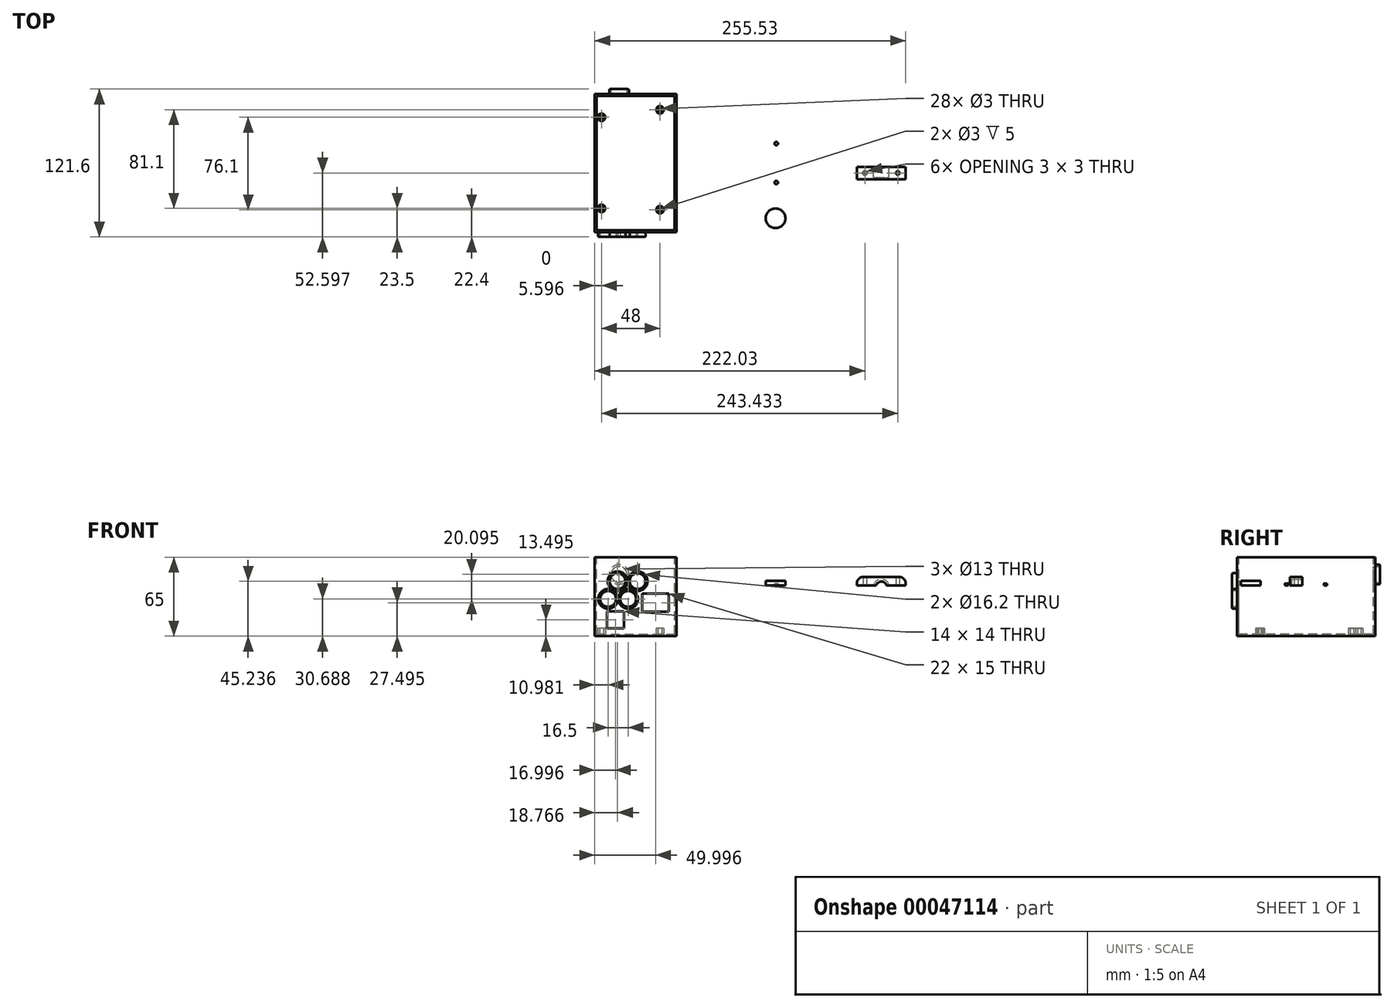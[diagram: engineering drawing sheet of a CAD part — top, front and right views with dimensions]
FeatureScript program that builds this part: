
annotation { "Feature Type Name" : "Feature", "Feature Type Description" : "" }
export const myFeature = defineFeature(function(context is Context, id is Id, definition is map)
    precondition{}
    {
        {
            assignVariable(context, id + "F0", {"name" : "width", "anyValue" : 1.6});
        }
        {
            var Q0;
            Q0=qCreatedBy(makeId("Front.planeOp"),FACE);
            var sketch = newSketch(context, id + "F1", { "sketchPlane" : qUnion([Q0])});
            skLineSegment(sketch, "E0.bottom", {"start": v(-41.87, 23.3) * mm, "end": v(25.33, 23.3) * mm});
            skLineSegment(sketch, "E0.top", {"start": v(-41.87, -41.7) * mm, "end": v(25.33, -41.7) * mm});
            skLineSegment(sketch, "E0.left", {"start": v(-41.87, 23.3) * mm, "end": v(-41.87, -41.7) * mm});
            skLineSegment(sketch, "E0.right", {"start": v(25.33, 23.3) * mm, "end": v(25.33, -41.7) * mm});
            skSolve(sketch);
        }
        {
            var Q0;
            Q0 = qSketchRegion(id + "F1", true);
            extrude(context, id + "F2", {"entities" : qUnion([Q0]), "depth" : 113.6 * mm});
        }
        {
            var Q0;
            Q0=makeQuery(id+"F2.opExtrude","SWEPT_FACE",FACE,{"disambiguationData":[OSD([sQuery(id+"F1.wireOp",EDGE,"E0.bottom")])]});
            var sketch = newSketch(context, id + "F3", { "sketchPlane" : qUnion([Q0])});
            skLineSegment(sketch, "E1.bottom", {"start": v(-40.27, -1.6) * mm, "end": v(23.73, -1.6) * mm});
            skLineSegment(sketch, "E1.top", {"start": v(-40.27, -112) * mm, "end": v(23.73, -112) * mm});
            skLineSegment(sketch, "E1.left", {"start": v(-40.27, -1.6) * mm, "end": v(-40.27, -112) * mm});
            skLineSegment(sketch, "E1.right", {"start": v(23.73, -1.6) * mm, "end": v(23.73, -112) * mm});
            skSolve(sketch);
        }
        {
            var Q0;
            Q0 = qSketchRegion(id + "F3", true);
            extrude(context, id + "F4", {"entities" : qUnion([Q0]), "operationType" : NewBodyOperationType.REMOVE, "oppositeDirection" : true, "depth" : (65 - getVariable(context, 'width')) * mm});
        }
        {
            var Q0;
            Q0=makeQuery(id+"F2.opExtrude","CAP_FACE",FACE,{"disambiguationData":[OSD([sQuery(id+"F1.wireOp",EDGE,"E0.bottom"),sQuery(id+"F1.wireOp",EDGE,"E0.top"),sQuery(id+"F1.wireOp",EDGE,"E0.left"),sQuery(id+"F1.wireOp",EDGE,"E0.right")])],"isStart":false});
            var sketch = newSketch(context, id + "F5", { "sketchPlane" : qUnion([Q0])});
            skLineSegment(sketch, "E2.bottom", {"start": v(-31.87, -21.2) * mm, "end": v(-17.87, -21.2) * mm});
            skLineSegment(sketch, "E2.top", {"start": v(-31.87, -35.2) * mm, "end": v(-17.87, -35.2) * mm});
            skLineSegment(sketch, "E2.left", {"start": v(-31.87, -21.2) * mm, "end": v(-31.87, -35.2) * mm});
            skLineSegment(sketch, "E2.right", {"start": v(-17.87, -21.2) * mm, "end": v(-17.87, -35.2) * mm});
            skLineSegment(sketch, "E3.bottom", {"start": v(-2.87, -6.7) * mm, "end": v(19.13, -6.7) * mm});
            skLineSegment(sketch, "E3.top", {"start": v(-2.87, -21.7) * mm, "end": v(19.13, -21.7) * mm});
            skLineSegment(sketch, "E3.left", {"start": v(-2.87, -6.7) * mm, "end": v(-2.87, -21.7) * mm});
            skLineSegment(sketch, "E3.right", {"start": v(19.13, -6.7) * mm, "end": v(19.13, -21.7) * mm});
            skCircle(sketch, "E4", {"center": v(-30.89, -11) * mm, "radius": 6.5 * mm});
            skCircle(sketch, "E5", {"center": v(-14.39, -11) * mm, "radius": 6.5 * mm});
            skCircle(sketch, "E6.MirrorC", {"center": v(-6.6, 3.55) * mm, "radius": 6.5 * mm});
            skCircle(sketch, "E7.MirrorC", {"center": v(-23.1, 3.55) * mm, "radius": 6.5 * mm});
            skCircle(sketch, "E8.0", {"center": v(-30.89, -11) * mm, "radius": 8.1 * mm});
            skCircle(sketch, "E9.0", {"center": v(-14.39, -11) * mm, "radius": 8.1 * mm});
            skCircle(sketch, "E10.0", {"center": v(-23.1, 3.55) * mm, "radius": 8.1 * mm});
            skCircle(sketch, "E11.0", {"center": v(-6.6, 3.55) * mm, "radius": 8.1 * mm});
            skSolve(sketch);
        }
        {
            var Q0;
            Q0=makeQuery(id+"F5.imprint","IMPRINT",FACE,{"disambiguationData":[TD([[makeQuery(id+"F5.imprint","IMPRINT",EDGE,{"derivedFrom":sQuery(id+"F5.wireOp",EDGE,"E3.bottom")}),-1.0]])]});
            var Q1;
            Q1=makeQuery(id+"F5.imprint","IMPRINT",FACE,{"disambiguationData":[TD([[makeQuery(id+"F5.imprint","IMPRINT",EDGE,{"derivedFrom":sQuery(id+"F5.wireOp",EDGE,"E2.bottom")}),-1.0]])]});
            var Q2;
            Q2=makeQuery(id+"F5.imprint","IMPRINT",FACE,{"disambiguationData":[TD([[makeQuery(id+"F5.imprint","IMPRINT",EDGE,{"derivedFrom":sQuery(id+"F5.wireOp",EDGE,"E5")}),1.0]])]});
            var Q3;
            Q3=makeQuery(id+"F5.imprint","IMPRINT",FACE,{"disambiguationData":[TD([[makeQuery(id+"F5.imprint","IMPRINT",EDGE,{"derivedFrom":sQuery(id+"F5.wireOp",EDGE,"E6.MirrorC")}),-1.0]])]});
            var Q4;
            Q4=makeQuery(id+"F5.imprint","IMPRINT",FACE,{"disambiguationData":[TD([[makeQuery(id+"F5.imprint","IMPRINT",EDGE,{"derivedFrom":sQuery(id+"F5.wireOp",EDGE,"E7.MirrorC")}),-1.0]])]});
            var Q5;
            Q5=makeQuery(id+"F5.imprint","IMPRINT",FACE,{"disambiguationData":[TD([[makeQuery(id+"F5.imprint","IMPRINT",EDGE,{"derivedFrom":sQuery(id+"F5.wireOp",EDGE,"E4")}),1.0]])]});
            extrude(context, id + "F6", {"entities" : qUnion([Q0, Q1, Q2, Q3, Q4, Q5]), "operationType" : NewBodyOperationType.REMOVE, "endBound" : BoundingType.UP_TO_NEXT, "oppositeDirection" : true, "depth" : 25 * mm});
        }
        {
            var Q0;
            Q0=makeQuery(id+"F5.imprint","IMPRINT",FACE,{"disambiguationData":[TD([[makeQuery(id+"F5.imprint","IMPRINT",EDGE,{"derivedFrom":sQuery(id+"F5.wireOp",EDGE,"E7.MirrorC")}),1.0]])]});
            var Q1;
            Q1=makeQuery(id+"F5.imprint","IMPRINT",FACE,{"disambiguationData":[TD([[makeQuery(id+"F5.imprint","IMPRINT",EDGE,{"derivedFrom":sQuery(id+"F5.wireOp",EDGE,"E6.MirrorC")}),1.0]])]});
            var Q2;
            Q2=makeQuery(id+"F5.imprint","IMPRINT",FACE,{"disambiguationData":[TD([[makeQuery(id+"F5.imprint","IMPRINT",EDGE,{"derivedFrom":sQuery(id+"F5.wireOp",EDGE,"E5")}),-1.0]])]});
            var Q3;
            Q3=makeQuery(id+"F5.imprint","IMPRINT",FACE,{"disambiguationData":[TD([[makeQuery(id+"F5.imprint","IMPRINT",EDGE,{"derivedFrom":sQuery(id+"F5.wireOp",EDGE,"E4")}),-1.0]])]});
            extrude(context, id + "F7", {"entities" : qUnion([Q0, Q1, Q2, Q3]), "operationType" : NewBodyOperationType.ADD, "depth" : 4 * mm});
        }
        {
            var Q0;
            Q0=makeQuery(id+"F7.opExtrude","CAP_FACE",FACE,{"disambiguationData":[OSD([sQuery(id+"F5.wireOp",EDGE,"E4"),sQuery(id+"F5.wireOp",EDGE,"E8.0")])],"isStart":false});
            var Q1;
            Q1=makeQuery(id+"F7.opExtrude","CAP_FACE",FACE,{"disambiguationData":[OSD([sQuery(id+"F5.wireOp",EDGE,"E7.MirrorC"),sQuery(id+"F5.wireOp",EDGE,"E10.0")])],"isStart":false});
            var Q2;
            Q2=makeQuery(id+"F7.opExtrude","CAP_FACE",FACE,{"disambiguationData":[OSD([sQuery(id+"F5.wireOp",EDGE,"E6.MirrorC"),sQuery(id+"F5.wireOp",EDGE,"E11.0")])],"isStart":false});
            var Q3;
            Q3=makeQuery(id+"F7.opExtrude","CAP_FACE",FACE,{"disambiguationData":[OSD([sQuery(id+"F5.wireOp",EDGE,"E5"),sQuery(id+"F5.wireOp",EDGE,"E9.0")])],"isStart":false});
            fillet(context, id + "F8", {"entities" : qUnion([Q0, Q1, Q2, Q3]), "radius" : 0.8 * mm, "tangentPropagation" : true, "allowEdgeOverflow" : false});
        }
        {
            var Q0;
            Q0=makeQuery(id+"F2.opExtrude","CAP_FACE",FACE,{"disambiguationData":[OSD([sQuery(id+"F1.wireOp",EDGE,"E0.bottom"),sQuery(id+"F1.wireOp",EDGE,"E0.top"),sQuery(id+"F1.wireOp",EDGE,"E0.left"),sQuery(id+"F1.wireOp",EDGE,"E0.right")])],"isStart":true});
            var sketch = newSketch(context, id + "F9", { "sketchPlane" : qUnion([Q0])});
            skCircle(sketch, "E12", {"center": v(21.87, 9.1) * mm, "radius": 6.5 * mm});
            skCircle(sketch, "E13.0", {"center": v(21.87, 9.1) * mm, "radius": 8.1 * mm});
            skSolve(sketch);
        }
        {
            var Q0;
            Q0=makeQuery(id+"F9.imprint","IMPRINT",FACE,{"disambiguationData":[TD([[makeQuery(id+"F9.imprint","IMPRINT",EDGE,{"derivedFrom":sQuery(id+"F9.wireOp",EDGE,"E12")}),1.0]])]});
            extrude(context, id + "F10", {"entities" : qUnion([Q0]), "operationType" : NewBodyOperationType.REMOVE, "endBound" : BoundingType.UP_TO_NEXT, "oppositeDirection" : true, "depth" : 25 * mm});
        }
        {
            var Q0;
            Q0=makeQuery(id+"F4.boolean.opBoolean","COPY",FACE,{"derivedFrom":makeQuery(id+"F4.opExtrude","CAP_FACE",FACE,{"disambiguationData":[OSD([sQuery(id+"F3.wireOp",EDGE,"E1.bottom"),sQuery(id+"F3.wireOp",EDGE,"E1.top"),sQuery(id+"F3.wireOp",EDGE,"E1.left"),sQuery(id+"F3.wireOp",EDGE,"E1.right")])],"isStart":false})});
            var sketch = newSketch(context, id + "F11", { "sketchPlane" : qUnion([Q0])});
            skCircle(sketch, "E14", {"center": v(-36.27, -94.1) * mm, "radius": 1.5 * mm});
            skCircle(sketch, "E15.0", {"center": v(-36.27, -94.1) * mm, "radius": 3.1 * mm});
            skCircle(sketch, "E16", {"center": v(11.73, -95.2) * mm, "radius": 1.5 * mm});
            skCircle(sketch, "E17.0", {"center": v(11.73, -95.2) * mm, "radius": 3.1 * mm});
            skCircle(sketch, "E18.0", {"center": v(-36.27, -19.1) * mm, "radius": 3.1 * mm});
            skCircle(sketch, "E19", {"center": v(-36.27, -19.1) * mm, "radius": 1.5 * mm});
            skCircle(sketch, "E20.0", {"center": v(11.73, -13) * mm, "radius": 3.1 * mm});
            skCircle(sketch, "E21", {"center": v(11.73, -13) * mm, "radius": 1.5 * mm});
            skSolve(sketch);
        }
        {
            var Q0;
            Q0 = qSketchRegion(id + "F11", true);
            extrude(context, id + "F12", {"entities" : qUnion([Q0]), "operationType" : NewBodyOperationType.ADD, "depth" : 5 * mm});
        }
        {
            var Q0;
            Q0=makeQuery(id+"F12.boolean.opBoolean","SPLIT",FACE,{"disambiguationData":[TD([makeQuery(id+"F12.opExtrude","SWEPT_FACE",FACE,{"disambiguationData":[OSD([sQuery(id+"F11.wireOp",EDGE,"E14")])]})])],"derivedFrom":makeQuery(id+"F4.boolean.opBoolean","COPY",FACE,{"derivedFrom":makeQuery(id+"F4.opExtrude","CAP_FACE",FACE,{"disambiguationData":[OSD([sQuery(id+"F3.wireOp",EDGE,"E1.bottom"),sQuery(id+"F3.wireOp",EDGE,"E1.top"),sQuery(id+"F3.wireOp",EDGE,"E1.left"),sQuery(id+"F3.wireOp",EDGE,"E1.right")])],"isStart":false})})});
            var Q1;
            Q1=makeQuery(id+"F12.boolean.opBoolean","SPLIT",FACE,{"disambiguationData":[TD([makeQuery(id+"F12.opExtrude","SWEPT_FACE",FACE,{"disambiguationData":[OSD([sQuery(id+"F11.wireOp",EDGE,"E21")])]})])],"derivedFrom":makeQuery(id+"F4.boolean.opBoolean","COPY",FACE,{"derivedFrom":makeQuery(id+"F4.opExtrude","CAP_FACE",FACE,{"disambiguationData":[OSD([sQuery(id+"F3.wireOp",EDGE,"E1.bottom"),sQuery(id+"F3.wireOp",EDGE,"E1.top"),sQuery(id+"F3.wireOp",EDGE,"E1.left"),sQuery(id+"F3.wireOp",EDGE,"E1.right")])],"isStart":false})})});
            extrude(context, id + "F13", {"entities" : qUnion([Q0, Q1]), "operationType" : NewBodyOperationType.REMOVE, "endBound" : BoundingType.UP_TO_NEXT, "oppositeDirection" : true, "depth" : 25 * mm});
        }
        {
            var Q0;
            Q0=makeQuery(id+"F9.imprint","IMPRINT",FACE,{"disambiguationData":[TD([[makeQuery(id+"F9.imprint","IMPRINT",EDGE,{"derivedFrom":sQuery(id+"F9.wireOp",EDGE,"E12")}),-1.0]])]});
            extrude(context, id + "F14", {"entities" : qUnion([Q0]), "operationType" : NewBodyOperationType.ADD, "depth" : 4 * mm});
        }
        {
            var Q0;
            Q0=makeQuery(id+"F14.opExtrude","CAP_FACE",FACE,{"disambiguationData":[OSD([sQuery(id+"F9.wireOp",EDGE,"E12"),sQuery(id+"F9.wireOp",EDGE,"E13.0")])],"isStart":false});
            fillet(context, id + "F15", {"entities" : qUnion([Q0]), "radius" : 0.8 * mm, "tangentPropagation" : true, "allowEdgeOverflow" : false});
        }
        {
            var Q0;
            Q0=qCreatedBy(makeId("Top.planeOp"),FACE);
            var sketch = newSketch(context, id + "F16", { "sketchPlane" : qUnion([Q0])});
            skLineSegment(sketch, "E22.bottom", {"start": v(57.75, 0) * mm, "end": v(124.95, 0) * mm, "construction": true});
            skLineSegment(sketch, "E22.top", {"start": v(57.75, -113.6) * mm, "end": v(124.95, -113.6) * mm, "construction": true});
            skLineSegment(sketch, "E22.left", {"start": v(57.75, 0) * mm, "end": v(57.75, -113.6) * mm, "construction": true});
            skLineSegment(sketch, "E22.right", {"start": v(124.95, 0) * mm, "end": v(124.95, -113.6) * mm, "construction": true});
            skLineSegment(sketch, "E23.0", {"start": v(55.95, -115.4) * mm, "end": v(126.75, -115.4) * mm});
            skLineSegment(sketch, "E23.1", {"start": v(55.95, 1.8) * mm, "end": v(55.95, -115.4) * mm});
            skLineSegment(sketch, "E23.2", {"start": v(55.95, 1.8) * mm, "end": v(126.75, 1.8) * mm});
            skLineSegment(sketch, "E23.3", {"start": v(126.75, 1.8) * mm, "end": v(126.75, -115.4) * mm});
            skLineSegment(sketch, "E24.0", {"start": v(57.55, 0.2) * mm, "end": v(125.15, 0.2) * mm});
            skLineSegment(sketch, "E24.1", {"start": v(57.55, 0.2) * mm, "end": v(57.55, -113.8) * mm});
            skLineSegment(sketch, "E24.2", {"start": v(57.55, -113.8) * mm, "end": v(125.15, -113.8) * mm});
            skLineSegment(sketch, "E24.3", {"start": v(125.15, 0.2) * mm, "end": v(125.15, -113.8) * mm});
            skLineSegment(sketch, "E25.0", {"start": v(59.35, -1.6) * mm, "end": v(123.35, -1.6) * mm, "construction": true});
            skLineSegment(sketch, "E25.1", {"start": v(59.35, -1.6) * mm, "end": v(59.35, -112) * mm, "construction": true});
            skLineSegment(sketch, "E25.2", {"start": v(59.35, -112) * mm, "end": v(123.35, -112) * mm, "construction": true});
            skLineSegment(sketch, "E25.3", {"start": v(123.35, -1.6) * mm, "end": v(123.35, -112) * mm, "construction": true});
            skLineSegment(sketch, "E26.0", {"start": v(123.15, -1.8) * mm, "end": v(123.15, -111.8) * mm});
            skLineSegment(sketch, "E26.1", {"start": v(59.55, -1.8) * mm, "end": v(123.15, -1.8) * mm});
            skLineSegment(sketch, "E26.2", {"start": v(59.55, -1.8) * mm, "end": v(59.55, -111.8) * mm});
            skLineSegment(sketch, "E26.3", {"start": v(59.55, -111.8) * mm, "end": v(123.15, -111.8) * mm});
            skLineSegment(sketch, "E27.0", {"start": v(121.55, -3.4) * mm, "end": v(121.55, -110.2) * mm});
            skLineSegment(sketch, "E27.1", {"start": v(61.15, -3.4) * mm, "end": v(121.55, -3.4) * mm});
            skLineSegment(sketch, "E27.2", {"start": v(61.15, -3.4) * mm, "end": v(61.15, -110.2) * mm});
            skLineSegment(sketch, "E27.3", {"start": v(61.15, -110.2) * mm, "end": v(121.55, -110.2) * mm});
            skSolve(sketch);
        }
        {
            var Q0;
            Q0=makeQuery(id+"F16.imprint","IMPRINT",FACE,{"disambiguationData":[TD([[makeQuery(id+"F16.imprint","IMPRINT",EDGE,{"derivedFrom":sQuery(id+"F16.wireOp",EDGE,"E27.0")}),-1.0]])]});
            var Q1;
            Q1=makeQuery(id+"F16.imprint","IMPRINT",FACE,{"disambiguationData":[TD([[makeQuery(id+"F16.imprint","IMPRINT",EDGE,{"derivedFrom":sQuery(id+"F16.wireOp",EDGE,"E26.0")}),-1.0]])]});
            var Q2;
            Q2=makeQuery(id+"F16.imprint","IMPRINT",FACE,{"disambiguationData":[TD([[makeQuery(id+"F16.imprint","IMPRINT",EDGE,{"derivedFrom":sQuery(id+"F16.wireOp",EDGE,"E24.0")}),-1.0]])]});
            var Q3;
            Q3=makeQuery(id+"F16.imprint","IMPRINT",FACE,{"disambiguationData":[TD([[makeQuery(id+"F16.imprint","IMPRINT",EDGE,{"derivedFrom":sQuery(id+"F16.wireOp",EDGE,"E23.0")}),1.0]])]});
            var Q4;
            Q4=sQuery(id+"F16.wireOp",EDGE,"E23.0");
            var Q5;
            Q5=sQuery(id+"F16.wireOp",EDGE,"E23.1");
            var Q6;
            Q6=sQuery(id+"F16.wireOp",EDGE,"E23.3");
            var Q7;
            Q7=sQuery(id+"F16.wireOp",EDGE,"E23.2");
            extrude(context, id + "F17", {"entities" : qUnion([Q0, Q1, Q2, Q3]), "surfaceEntities" : qUnion([Q4, Q5, Q6, Q7]), "depth" : (getVariable(context, 'width')) * mm});
        }
        {
            var Q0;
            Q0=makeQuery(id+"F16.imprint","IMPRINT",FACE,{"disambiguationData":[TD([[makeQuery(id+"F16.imprint","IMPRINT",EDGE,{"derivedFrom":sQuery(id+"F16.wireOp",EDGE,"E23.0")}),1.0]])]});
            var Q1;
            Q1=makeQuery(id+"F16.imprint","IMPRINT",FACE,{"disambiguationData":[TD([[makeQuery(id+"F16.imprint","IMPRINT",EDGE,{"derivedFrom":sQuery(id+"F16.wireOp",EDGE,"E26.0")}),-1.0]])]});
            extrude(context, id + "F18", {"entities" : qUnion([Q0, Q1]), "operationType" : NewBodyOperationType.ADD, "depth" : (5 + getVariable(context, 'width')) * mm});
        }
        {
            var Q0;
            Q0=makeQuery(id+"F17.opExtrude","CAP_FACE",FACE,{"disambiguationData":[OSD([sQuery(id+"F16.wireOp",EDGE,"E23.0"),sQuery(id+"F16.wireOp",EDGE,"E23.1"),sQuery(id+"F16.wireOp",EDGE,"E23.2"),sQuery(id+"F16.wireOp",EDGE,"E23.3")])],"isStart":true});
            var sketch = newSketch(context, id + "F19", { "sketchPlane" : qUnion([Q0])});
            skLineSegment(sketch, "E28.bottom", {"start": v(71.35, 76.8) * mm, "end": v(111.35, 76.8) * mm, "construction": true});
            skLineSegment(sketch, "E28.top", {"start": v(71.35, 36.8) * mm, "end": v(111.35, 36.8) * mm, "construction": true});
            skLineSegment(sketch, "E28.left", {"start": v(71.35, 76.8) * mm, "end": v(71.35, 36.8) * mm, "construction": true});
            skLineSegment(sketch, "E28.right", {"start": v(111.35, 76.8) * mm, "end": v(111.35, 36.8) * mm, "construction": true});
            skLineSegment(sketch, "E29", {"start": v(91.35, 115.4) * mm, "end": v(91.35, -1.8) * mm, "construction": true});
            skLineSegment(sketch, "E30", {"start": v(55.95, 56.8) * mm, "end": v(126.75, 56.8) * mm, "construction": true});
            skCircle(sketch, "E31", {"center": v(75.35, 72.8) * mm, "radius": 1.4 * mm});
            skCircle(sketch, "E32", {"center": v(75.35, 40.8) * mm, "radius": 1.4 * mm});
            skCircle(sketch, "E33.MirrorC", {"center": v(107.35, 40.8) * mm, "radius": 1.4 * mm});
            skCircle(sketch, "E34.MirrorC", {"center": v(107.35, 72.8) * mm, "radius": 1.4 * mm});
            skCircle(sketch, "E35", {"center": v(91.35, 56.8) * mm, "radius": 18 * mm});
            skCircle(sketch, "E36", {"center": v(106.75, 102.2) * mm, "radius": 6.5 * mm});
            skSolve(sketch);
        }
        {
            var Q0;
            Q0=makeQuery(id+"F19.imprint","IMPRINT",FACE,{"disambiguationData":[TD([[makeQuery(id+"F19.imprint","IMPRINT",EDGE,{"derivedFrom":sQuery(id+"F19.wireOp",EDGE,"E35")}),1.0]])]});
            var Q1;
            Q1=makeQuery(id+"F19.imprint","IMPRINT",FACE,{"disambiguationData":[TD([[makeQuery(id+"F19.imprint","IMPRINT",EDGE,{"derivedFrom":sQuery(id+"F19.wireOp",EDGE,"E31")}),1.0]])]});
            var Q2;
            Q2=makeQuery(id+"F19.imprint","IMPRINT",FACE,{"disambiguationData":[TD([[makeQuery(id+"F19.imprint","IMPRINT",EDGE,{"derivedFrom":sQuery(id+"F19.wireOp",EDGE,"E32")}),1.0]])]});
            var Q3;
            Q3=makeQuery(id+"F19.imprint","IMPRINT",FACE,{"disambiguationData":[TD([[makeQuery(id+"F19.imprint","IMPRINT",EDGE,{"derivedFrom":sQuery(id+"F19.wireOp",EDGE,"E33.MirrorC")}),-1.0]])]});
            var Q4;
            Q4=makeQuery(id+"F19.imprint","IMPRINT",FACE,{"disambiguationData":[TD([[makeQuery(id+"F19.imprint","IMPRINT",EDGE,{"derivedFrom":sQuery(id+"F19.wireOp",EDGE,"E34.MirrorC")}),-1.0]])]});
            var Q5;
            Q5=makeQuery(id+"F19.imprint","IMPRINT",FACE,{"disambiguationData":[TD([[makeQuery(id+"F19.imprint","IMPRINT",EDGE,{"derivedFrom":sQuery(id+"F19.wireOp",EDGE,"E36")}),1.0]])]});
            extrude(context, id + "F20", {"entities" : qUnion([Q0, Q1, Q2, Q3, Q4, Q5]), "operationType" : NewBodyOperationType.REMOVE, "endBound" : BoundingType.UP_TO_NEXT, "oppositeDirection" : true, "depth" : 25 * mm});
        }
        {
            var Q0;
            Q0=makeQuery(id+"F17.opExtrude","CAP_FACE",FACE,{"disambiguationData":[OSD([sQuery(id+"F16.wireOp",EDGE,"E23.0"),sQuery(id+"F16.wireOp",EDGE,"E23.1"),sQuery(id+"F16.wireOp",EDGE,"E23.2"),sQuery(id+"F16.wireOp",EDGE,"E23.3")])],"isStart":true});
            var sketch = newSketch(context, id + "F21", { "sketchPlane" : qUnion([Q0])});
            skCircle(sketch, "E37.0", {"center": v(106.75, 102.2) * mm, "radius": 8.1 * mm});
            skSolve(sketch);
        }
        {
            var Q0;
            Q0=makeQuery(id+"F21.imprint","IMPRINT",FACE,{"disambiguationData":[TD([[makeQuery(id+"F21.imprint","IMPRINT",EDGE,{"derivedFrom":sQuery(id+"F21.wireOp",EDGE,"E37.0")}),1.0]])]});
            extrude(context, id + "F22", {"entities" : qUnion([Q0]), "operationType" : NewBodyOperationType.ADD, "oppositeDirection" : true, "depth" : 4 * mm});
        }
        {
            var Q0;
            Q0=qCreatedBy(makeId("Top.planeOp"),FACE);
            var sketch = newSketch(context, id + "F23", { "sketchPlane" : qUnion([Q0])});
            skLineSegment(sketch, "E38.bottom", {"start": v(173.66, -60) * mm, "end": v(213.66, -60) * mm});
            skLineSegment(sketch, "E38.top", {"start": v(173.66, -70) * mm, "end": v(213.66, -70) * mm});
            skLineSegment(sketch, "E38.left", {"start": v(173.66, -60) * mm, "end": v(173.66, -70) * mm});
            skLineSegment(sketch, "E38.right", {"start": v(213.66, -60) * mm, "end": v(213.66, -70) * mm});
            skCircle(sketch, "E39", {"center": v(180.16, -65) * mm, "radius": 1.5 * mm});
            skCircle(sketch, "E40", {"center": v(207.16, -65) * mm, "radius": 1.5 * mm});
            skSolve(sketch);
        }
        {
            var Q0;
            Q0=makeQuery(id+"F23.imprint","IMPRINT",FACE,{"disambiguationData":[TD([[makeQuery(id+"F23.imprint","IMPRINT",EDGE,{"derivedFrom":sQuery(id+"F23.wireOp",EDGE,"E38.bottom")}),-1.0]])]});
            extrude(context, id + "F24", {"entities" : qUnion([Q0]), "depth" : 7 * mm});
        }
        {
            var Q0;
            Q0=makeQuery(id+"F24.opExtrude","SWEPT_FACE",FACE,{"disambiguationData":[OSD([sQuery(id+"F23.wireOp",EDGE,"E38.bottom")])]});
            var sketch = newSketch(context, id + "F25", { "sketchPlane" : qUnion([Q0])});
            skCircle(sketch, "E41", {"center": v(-193.66, -1.3) * mm, "radius": 6.5 * mm});
            skCircle(sketch, "E42.0", {"center": v(-193.66, -1.3) * mm, "radius": 4.5 * mm});
            skSolve(sketch);
        }
        {
            var Q0;
            {var subQ0=sQuery(id+"F25.wireOp",EDGE,"E42.0");var subQ1=makeQuery(id+"F24.opExtrude","CAP_EDGE",EDGE,{"disambiguationData":[OSD([sQuery(id+"F23.wireOp",EDGE,"E38.bottom")])],"isStart":true});var subQ2=makeQuery(id+"F25.imprint","INTERSECT",VERTEX,{"disambiguationData":[OD(0.0)],"derivedFrom":[subQ1,subQ0]});Q0=makeQuery(id+"F25.imprint","IMPRINT",FACE,{"disambiguationData":[TD([[makeQuery(id+"F25.imprint","IMPRINT",EDGE,{"disambiguationData":[TD([[subQ2,-1.0]])],"derivedFrom":subQ0}),1.0]])]});}
            extrude(context, id + "F26", {"entities" : qUnion([Q0]), "operationType" : NewBodyOperationType.REMOVE, "endBound" : BoundingType.UP_TO_NEXT, "oppositeDirection" : true, "depth" : 8 * mm});
        }
        {
            var Q0;
            {var subQ0=sQuery(id+"F25.wireOp",EDGE,"E41");var subQ1=makeQuery(id+"F24.opExtrude","CAP_EDGE",EDGE,{"disambiguationData":[OSD([sQuery(id+"F23.wireOp",EDGE,"E38.bottom")])],"isStart":true});var subQ2=makeQuery(id+"F25.imprint","INTERSECT",VERTEX,{"disambiguationData":[OD(0.0)],"derivedFrom":[subQ1,subQ0]});Q0=makeQuery(id+"F25.imprint","IMPRINT",FACE,{"disambiguationData":[TD([[makeQuery(id+"F25.imprint","IMPRINT",EDGE,{"disambiguationData":[TD([[subQ2,-1.0]])],"derivedFrom":subQ0}),1.0]])]});}
            extrude(context, id + "F27", {"entities" : qUnion([Q0]), "operationType" : NewBodyOperationType.REMOVE, "oppositeDirection" : true, "depth" : (10 - 1.5) * mm});
        }
        {
            var Q0;
            Q0=makeQuery(id+"F24.opExtrude","CAP_EDGE",EDGE,{"disambiguationData":[OSD([sQuery(id+"F23.wireOp",EDGE,"E38.right")])],"isStart":false});
            var Q1;
            Q1=makeQuery(id+"F24.opExtrude","CAP_EDGE",EDGE,{"disambiguationData":[OSD([sQuery(id+"F23.wireOp",EDGE,"E38.left")])],"isStart":false});
            fillet(context, id + "F28", {"entities" : qUnion([Q0, Q1]), "radius" : 5 * mm, "tangentPropagation" : true, "allowEdgeOverflow" : false});
        }
    });
